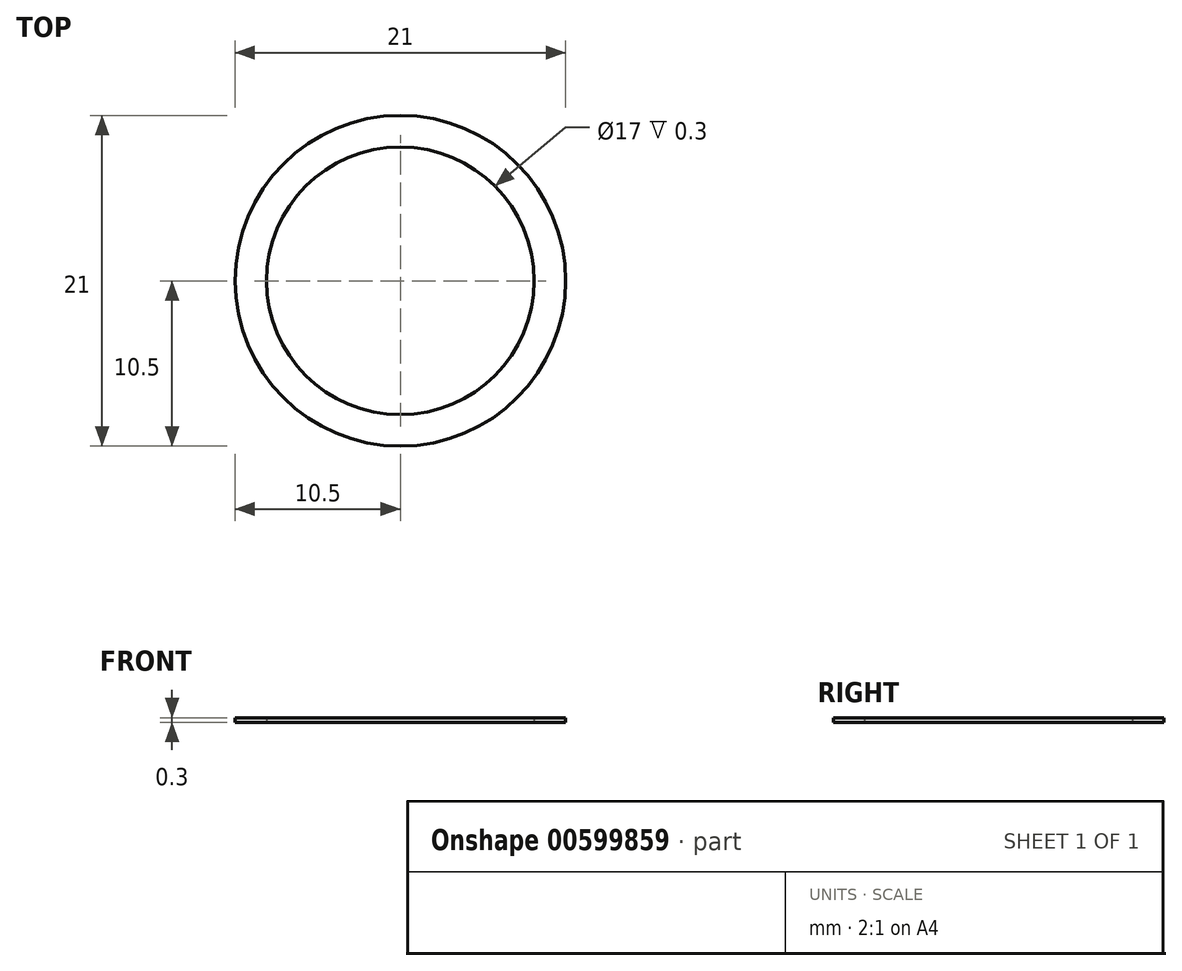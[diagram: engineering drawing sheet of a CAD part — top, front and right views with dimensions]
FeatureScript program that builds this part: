
annotation { "Feature Type Name" : "Feature", "Feature Type Description" : "" }
export const myFeature = defineFeature(function(context is Context, id is Id, definition is map)
    precondition{}
    {
        {
            var Q0;
            Q0=qCreatedBy(makeId("Top.planeOp"),FACE);
            var sketch = newSketch(context, id + "F0", { "sketchPlane" : qUnion([Q0])});
            skCircle(sketch, "E0", {"center": v(0, 0) * mm, "radius": 10.5 * mm});
            skCircle(sketch, "E1", {"center": v(0, 0) * mm, "radius": 8.5 * mm});
            skSolve(sketch);
        }
        {
            var Q0;
            Q0=makeQuery(id+"F0.imprint","IMPRINT",FACE,{"disambiguationData":[TD([[makeQuery(id+"F0.imprint","IMPRINT",EDGE,{"derivedFrom":sQuery(id+"F0.wireOp",EDGE,"E0")}),1.0]])]});
            extrude(context, id + "F1", {"entities" : qUnion([Q0]), "depth" : 0.3 * mm, "offsetDistance" : 25 * mm});
        }
    });
